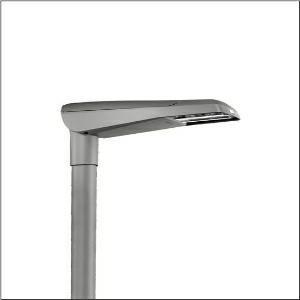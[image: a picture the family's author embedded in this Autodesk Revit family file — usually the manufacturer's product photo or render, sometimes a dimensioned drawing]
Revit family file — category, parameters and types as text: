
# Revit family: streetlight_sl_11_iq_micro___st1_2a_5xc1a21f08ce_ee83
name_source: partatom
category: Lighting Fixtures
units: mm (PartAtom-declared; Revit-internal decimal feet)

## family parameters
Cut with Voids When Loaded = No
Host = Face
Light Source = No
Part Type = Normal
Room Calculation Point = No
Round Connector Dimension = Use Diameter
Shared = No

## types (1)
- --- (1 x LED, 1540 lm, 12.6 W, 2200K)
    Apparent Load = 13 VA
    CIE Flux Codes = 33 71 96 100 100
    Color Rendering = 70
    Color Temperature = 2200K
    Default Elevation = 1800 mm
    Description = Streetlight SL 11 iQ micro, mast luminaire, primary light control with 3 zone facetted reflector, of plastic, silver coated, highly specular, primary optical cover: cover, of PMMA, transparent, light distribution: ST1.2a, light emission: direct distribution, primary light characteristic: asymmetric, installation type: post-top, side-entry, lamps: LED, High Power LED, rated values: 1.540lm | 12,6W | 122,2lm/W (begin service life); end service life: 1.540lm | 12,9W; at 50% lumin. flux: 770lm | 6,8W | 113,2lm/W, colour temperature: 2200K, colour rendering: CRI > 70, light colour: 722, light setting 1 begin service life: 100% | 1.540lm | 12,6W | 122,2lm/W | 2.200K, light setting 1 end service life: 12,9W, further light settings possible, control: Street-Remote, optimised constant luminous flux control (CLO 2.0), Desk-Remote (wireless, voltage-free reading and setting of iQ features in the workshop via application-optimized NFC function/RFID function), Light-Fading, Smart-Wire, Night-Set, Lumen-Switch, Temp-Guard, Auto-Match, with cable H07RN-F 5x 1.5mm², mains connection: 230..240V, AC, 50/60Hz, connection cable pre-assembled, cable length: 5,5m, luminaire housing, of diecast aluminium, powder-coated, Siteco® metallic grey (DB 702S), please order mast flange separately, inclination adjustable without tools: 0°, 5°, 10°, 15° (post-top) | 0°, -5°, -10°, -15° (side-entry), sealing non-destructively replaceable, multi-level sealing system, length: 600mm, width: 174mm, height: 116mm, mast flange for spigot size: 42mm (side-entry): 5XC10008XM4, 60/48mm (side-entry/post-top): 5XC10108XM2, 76/60mm (side-entry/post-top): 5XC10108XM1, equipment: standard, protection rating (complete): IP66, insulation class (complete): insulation class II (safety insulation), certification: CE, ENEC, ENEC+, VDE, impact resistance: IK10, permissible operating ambient temperature for outdoor applications: -25..+50°C, standard-compliant lighting for roads and squares, Environmental Product Declaration (EPD) tested and certified by an independent institute, packaging unit: 1 piece

Light Distribution: ST1.2a
    Height = 116 mm
    Lamp = 1 x LED
    Lamp Light Flux = 1540 lm
    Lamp Power = 12.6 W
    Lamp count = 1
    Length = 600 mm
    Luminous efficacy = 122 lm/W
    Manufacturer = Siteco
    ModVariant = No
    Model = 5XC1A21F08CE
    Number of Poles = 1
    OnlyDefault = Yes
    Power Factor = 1
    Product Name = Streetlight SL 11 iQ micro | ST1.2a
    Product group = mast luminaire | pylon top
    ProductGroupID = 6100
    Protection Class = Protection class II
    Protection Degree = IP 66
    RLX_Detail_Level = 1
    RLX_Emergency_Light_Flux = 0 lm
    RLX_Emergency_Type = 0
    RLX_Emergency_Type_DB = No
    RlxData = <blob elided: 26525 chars, md5=63b50c03>
    Socket = socket
    Standby Power = 0 W
    System Light Flux = 1540 lm
    System Power = 13 W
    Type Comments = factory setting: luminous flux: 100 % | dim-lin: 254 | 229 mA
    Type Image = l_1006566.jpg
    URL = http://relux.com
    VarID = @adj_000891
    Voltage = 0 V
    Weight = 0.00 kg
    Width = 174 mm

## geometry (parser evidence)
native form markers: Blend x4, Sweep x11
no freeform markers — native parametric forms only
